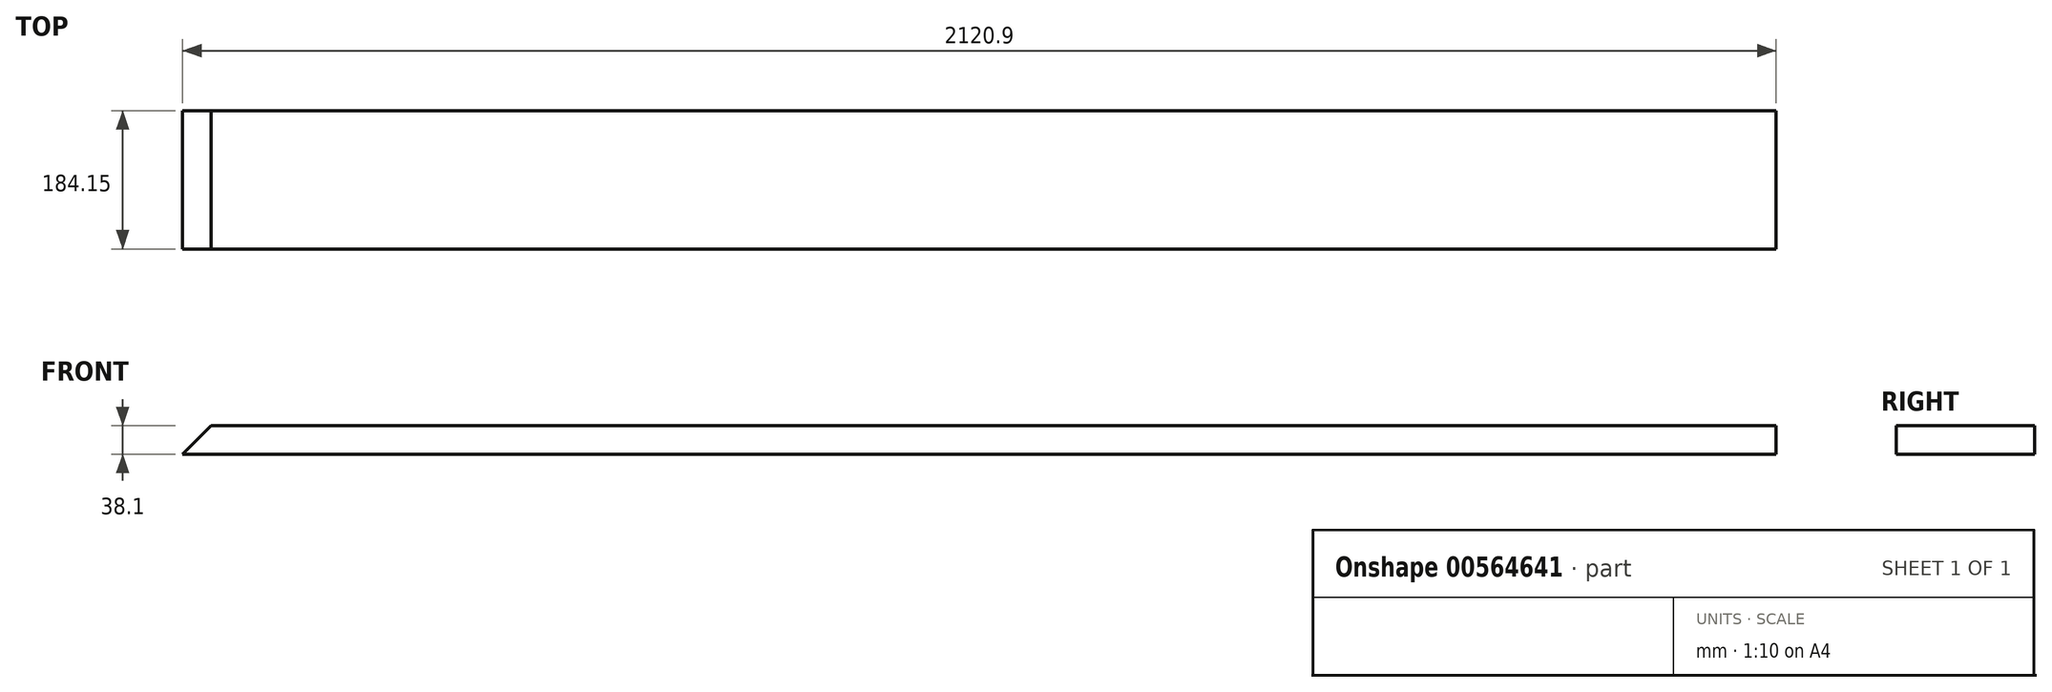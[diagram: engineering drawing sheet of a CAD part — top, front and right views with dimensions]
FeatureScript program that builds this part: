
annotation { "Feature Type Name" : "Feature", "Feature Type Description" : "" }
export const myFeature = defineFeature(function(context is Context, id is Id, definition is map)
    precondition{}
    {
        {
            var Q0;
            Q0=qCreatedBy(makeId("Top.planeOp"),FACE);
            var sketch = newSketch(context, id + "F0", { "sketchPlane" : qUnion([Q0])});
            skLineSegment(sketch, "E0.bottom", {"start": v(0, 0) * mm, "end": v(2120.9, 0) * mm});
            skLineSegment(sketch, "E0.top", {"start": v(0, 184.15) * mm, "end": v(2120.9, 184.15) * mm});
            skLineSegment(sketch, "E0.left", {"start": v(0, 0) * mm, "end": v(0, 184.15) * mm});
            skLineSegment(sketch, "E0.right", {"start": v(2120.9, 0) * mm, "end": v(2120.9, 184.15) * mm});
            skSolve(sketch);
        }
        {
            var Q0;
            Q0=makeQuery(id+"F0.imprint","IMPRINT",FACE,{"disambiguationData":[TD([[makeQuery(id+"F0.imprint","IMPRINT",EDGE,{"derivedFrom":sQuery(id+"F0.wireOp",EDGE,"E0.bottom")}),1.0]])]});
            extrude(context, id + "F1", {"entities" : qUnion([Q0]), "depth" : 38.1 * mm, "offsetDistance" : 25.4 * mm});
        }
        {
            var Q0;
            Q0=makeQuery(id+"F1.opExtrude","SWEPT_FACE",FACE,{"disambiguationData":[OSD([sQuery(id+"F0.wireOp",EDGE,"E0.top")])]});
            var sketch = newSketch(context, id + "F2", { "sketchPlane" : qUnion([Q0])});
            skLineSegment(sketch, "E1", {"start": v(0, 38.1) * mm, "end": v(0, 0) * mm});
            skLineSegment(sketch, "E2", {"start": v(0, 0) * mm, "end": v(-38.1, 38.1) * mm});
            skLineSegment(sketch, "E3", {"start": v(-38.1, 38.1) * mm, "end": v(0, 38.1) * mm});
            skSolve(sketch);
        }
        {
            var Q0;
            Q0=makeQuery(id+"F2.imprint","IMPRINT",FACE,{"disambiguationData":[TD([[makeQuery(id+"F2.imprint","IMPRINT",EDGE,{"derivedFrom":sQuery(id+"F2.wireOp",EDGE,"E1")}),-1.0]])]});
            extrude(context, id + "F3", {"entities" : qUnion([Q0]), "operationType" : NewBodyOperationType.REMOVE, "oppositeDirection" : true, "depth" : 254 * mm, "offsetDistance" : 25.4 * mm});
        }
    });
